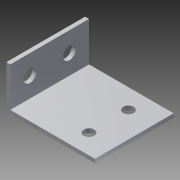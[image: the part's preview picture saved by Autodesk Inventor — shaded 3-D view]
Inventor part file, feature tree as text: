
AUTODESK INVENTOR PART (.ipt)
format: ipt  version: 2015 (Build 190159000, 159)  size: 128,512 bytes
history: native  units: mm
features: sketch x4, extrude x2, hole x2
ambient origin geometry x8: Origin, YZ Plane, XZ Plane, XY Plane, X Axis, Y Axis, Z Axis, Center Point
bodies: Body1 (feature_tree)
feature tree (8):
  extrude  "押し出し2"  Depth=22.5mm
  hole  "穴2"  [1 undecoded]
  extrude  "押し出し3"  Depth=1.0mm TaperAngle=0.0deg
  hole  "穴3"  [1 undecoded]
  sketch  "スケッチ3"
  sketch  "スケッチ4"
  sketch  "スケッチ5"
  sketch  "スケッチ6"
note: 2 required parameter values undecoded (feature->parameter linkage not recoverable at this tier; creation-order binding heuristic only, values carry confidence <= 0.55)
